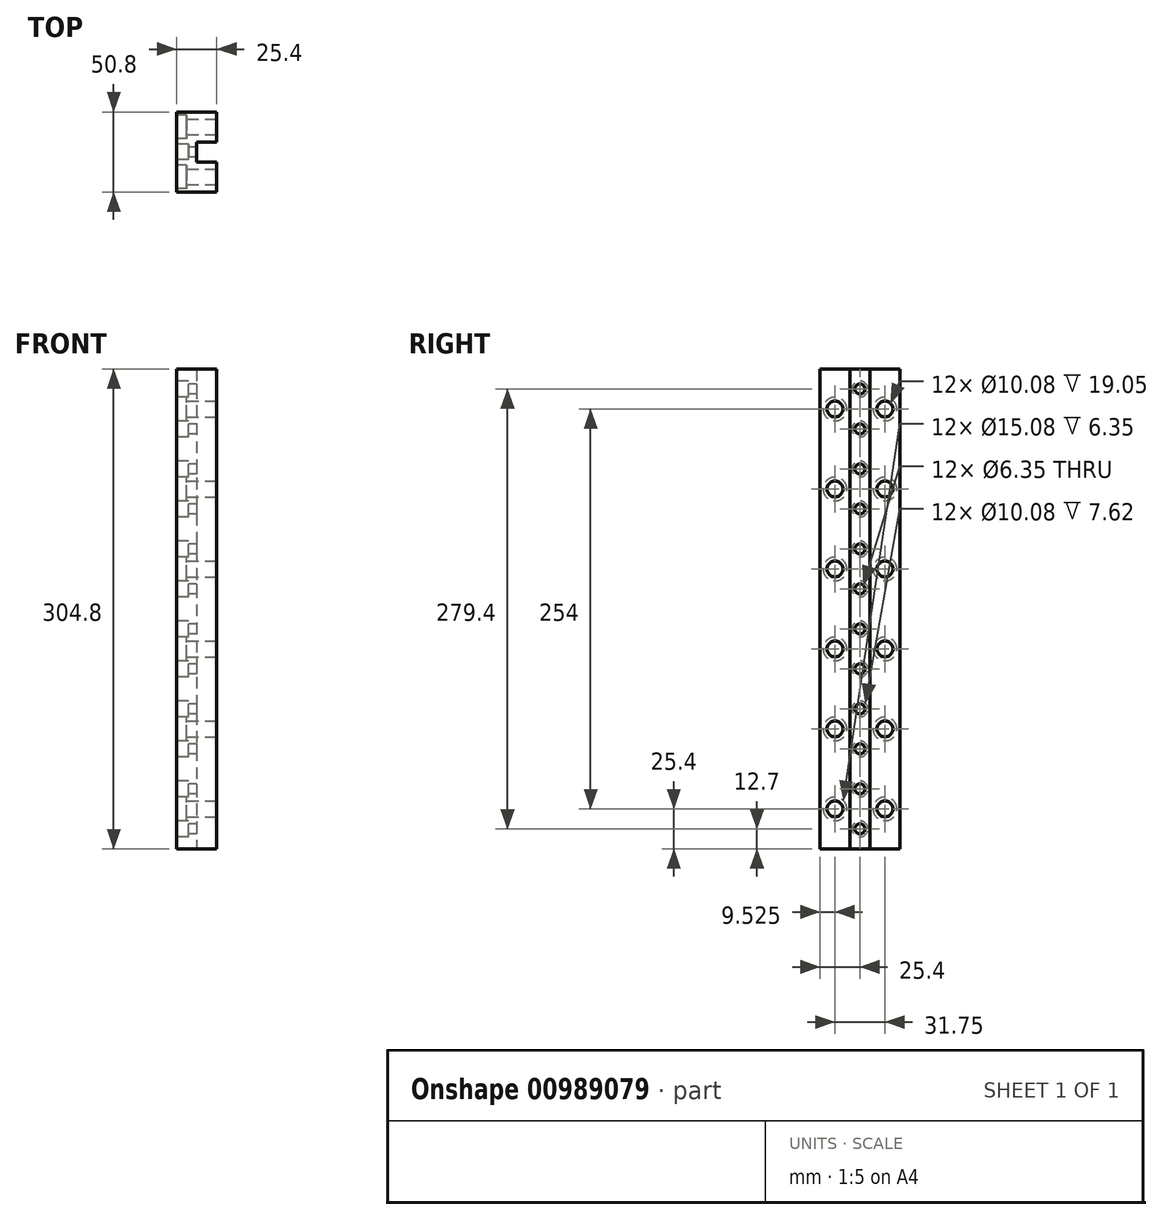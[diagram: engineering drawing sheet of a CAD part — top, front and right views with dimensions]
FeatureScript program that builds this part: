
annotation { "Feature Type Name" : "Feature", "Feature Type Description" : "" }
export const myFeature = defineFeature(function(context is Context, id is Id, definition is map)
    precondition{}
    {
        {
            var Q0;
            Q0=qCreatedBy(makeId("Right.planeOp"),FACE);
            var sketch = newSketch(context, id + "F0", { "sketchPlane" : qUnion([Q0])});
            skLineSegment(sketch, "E0.bottom", {"start": v(-25.4, 152.4) * mm, "end": v(25.4, 152.4) * mm});
            skLineSegment(sketch, "E0.top", {"start": v(-25.4, -152.4) * mm, "end": v(25.4, -152.4) * mm});
            skLineSegment(sketch, "E0.left", {"start": v(-25.4, 152.4) * mm, "end": v(-25.4, -152.4) * mm});
            skLineSegment(sketch, "E0.right", {"start": v(25.4, 152.4) * mm, "end": v(25.4, -152.4) * mm});
            skPoint(sketch, "E0.middle", {"position": v(0, 0) * mm});
            skSolve(sketch);
        }
        {
            var Q0;
            Q0 = qSketchRegion(id + "F0", true);
            extrude(context, id + "F1", {"entities" : qUnion([Q0]), "endBound" : BoundingType.SYMMETRIC, "depth" : 25.4 * mm, "offsetDistance" : 25.4 * mm});
        }
        {
            var Q0;
            Q0=qCreatedBy(makeId("Top.planeOp"),FACE);
            cPlane(context, id + "F2", {"entities" : qUnion([Q0]), "cplaneType" : CPlaneType.OFFSET, "offset" : 152.4 * mm, "oppositeDirection" : true, "width" : 152.4 * mm, "height" : 152.4 * mm});
        }
        {
            var Q0;
            Q0=qCreatedBy(id+"F2.planeOp",FACE);
            var sketch = newSketch(context, id + "F3", { "sketchPlane" : qUnion([Q0])});
            skLineSegment(sketch, "E1.bottom", {"start": v(12.7, -6.35) * mm, "end": v(0, -6.35) * mm});
            skLineSegment(sketch, "E1.top", {"start": v(12.7, 6.35) * mm, "end": v(0, 6.35) * mm});
            skLineSegment(sketch, "E1.left", {"start": v(12.7, -6.35) * mm, "end": v(12.7, 6.35) * mm});
            skLineSegment(sketch, "E1.right", {"start": v(0, -6.35) * mm, "end": v(0, 6.35) * mm});
            skPoint(sketch, "E2", {"position": v(0, -25.4) * mm});
            skPoint(sketch, "E3", {"position": v(0, 25.4) * mm});
            skSolve(sketch);
        }
        {
            var Q0;
            Q0 = qSketchRegion(id + "F3", true);
            extrude(context, id + "F4", {"entities" : qUnion([Q0]), "operationType" : NewBodyOperationType.REMOVE, "depth" : 304.8 * mm, "offsetDistance" : 25.4 * mm});
        }
        {
            var Q0;
            Q0=qCreatedBy(makeId("Right.planeOp"),FACE);
            cPlane(context, id + "F5", {"entities" : qUnion([Q0]), "cplaneType" : CPlaneType.OFFSET, "offset" : 12.7 * mm, "width" : 152.4 * mm, "height" : 152.4 * mm});
        }
        {
            var Q0;
            Q0=qCreatedBy(id+"F5.planeOp",FACE);
            var sketch = newSketch(context, id + "F6", { "sketchPlane" : qUnion([Q0])});
            skPoint(sketch, "E4", {"position": v(-25.4, -152.4) * mm});
            skPoint(sketch, "E5", {"position": v(-6.35, -152.4) * mm});
            skPoint(sketch, "E6", {"position": v(6.35, -152.4) * mm});
            skPoint(sketch, "E7", {"position": v(25.4, -152.4) * mm});
            skPoint(sketch, "E8", {"position": v(-25.4, -101.6) * mm});
            skPoint(sketch, "E9", {"position": v(-6.35, -101.6) * mm});
            skPoint(sketch, "E10", {"position": v(6.35, -101.6) * mm});
            skPoint(sketch, "E11", {"position": v(25.4, -101.6) * mm});
            skPoint(sketch, "E12", {"position": v(-25.4, -50.8) * mm});
            skPoint(sketch, "E13", {"position": v(-6.35, -50.8) * mm});
            skPoint(sketch, "E14", {"position": v(6.35, -50.8) * mm});
            skPoint(sketch, "E15", {"position": v(25.4, -50.8) * mm});
            skPoint(sketch, "E16", {"position": v(-25.4, 0) * mm});
            skPoint(sketch, "E17", {"position": v(-6.35, 0) * mm});
            skPoint(sketch, "E18", {"position": v(6.35, 0) * mm});
            skPoint(sketch, "E19", {"position": v(25.4, 0) * mm});
            skPoint(sketch, "E20", {"position": v(-25.4, 50.8) * mm});
            skPoint(sketch, "E21", {"position": v(-6.35, 50.8) * mm});
            skPoint(sketch, "E22", {"position": v(6.35, 50.8) * mm});
            skPoint(sketch, "E23", {"position": v(25.4, 50.8) * mm});
            skPoint(sketch, "E24", {"position": v(-25.4, 101.6) * mm});
            skPoint(sketch, "E25", {"position": v(-6.35, 101.6) * mm});
            skPoint(sketch, "E26", {"position": v(6.35, 101.6) * mm});
            skPoint(sketch, "E27", {"position": v(25.4, 101.6) * mm});
            skPoint(sketch, "E28", {"position": v(-15.88, -76.2) * mm});
            skPoint(sketch, "E29", {"position": v(-15.88, -25.4) * mm});
            skPoint(sketch, "E30", {"position": v(-15.88, 25.4) * mm});
            skPoint(sketch, "E31", {"position": v(-15.88, 76.2) * mm});
            skPoint(sketch, "E32", {"position": v(15.87, 76.2) * mm});
            skPoint(sketch, "E33", {"position": v(15.87, 25.4) * mm});
            skPoint(sketch, "E34", {"position": v(15.87, -25.4) * mm});
            skPoint(sketch, "E35", {"position": v(15.87, -76.2) * mm});
            skPoint(sketch, "E36", {"position": v(-15.88, -127) * mm});
            skPoint(sketch, "E37", {"position": v(-15.88, -152.4) * mm});
            skPoint(sketch, "E38", {"position": v(15.87, -127) * mm});
            skPoint(sketch, "E39", {"position": v(15.87, -152.4) * mm});
            skPoint(sketch, "E40", {"position": v(-15.88, 127) * mm});
            skPoint(sketch, "E41", {"position": v(15.87, 127) * mm});
            skSolve(sketch);
        }
        {
            var Q0;
            Q0=sQuery(id+"F6.wireOp",VERTEX,"d55c85b4-804a-40fe-89ae-485f87a3ce57");
            var Q1;
            Q1=sQuery(id+"F6.wireOp",VERTEX,"4aae8de5-d04d-4cfe-9f82-e7af8451480e");
            var Q2;
            Q2=sQuery(id+"F6.wireOp",VERTEX,"14c4b5a4-c554-4fe2-9cf0-08c26e14d046");
            var Q3;
            Q3=sQuery(id+"F6.wireOp",VERTEX,"b5e11202-0810-44d7-ac35-54ce5016bb80");
            var Q4;
            Q4=sQuery(id+"F6.wireOp",VERTEX,"21e4fa36-830b-4be3-85d7-d00b1b71e43a");
            var Q5;
            Q5=sQuery(id+"F6.wireOp",VERTEX,"086ac343-482b-45e4-8ac3-c1544311829b");
            var Q6;
            Q6=sQuery(id+"F6.wireOp",VERTEX,"6163d127-73d7-440f-8c50-218c48537137");
            var Q7;
            Q7=sQuery(id+"F6.wireOp",VERTEX,"6c5e894b-45dd-4a6c-a4cd-9d038fab3ba1");
            var Q8;
            Q8=sQuery(id+"F6.wireOp",VERTEX,"e5a3135e-7f6b-4397-8038-c7202fe8f8f5");
            var Q9;
            Q9=sQuery(id+"F6.wireOp",VERTEX,"4baa1079-f2f2-408e-9dee-b537d3760503");
            var Q10;
            Q10=sQuery(id+"F6.wireOp",VERTEX,"E31");
            var Q11;
            Q11=sQuery(id+"F6.wireOp",VERTEX,"E32");
            var Q12;
            Q12=sQuery(id+"F6.wireOp",VERTEX,"E33");
            var Q13;
            Q13=sQuery(id+"F6.wireOp",VERTEX,"E30");
            var Q14;
            Q14=sQuery(id+"F6.wireOp",VERTEX,"E29");
            var Q15;
            Q15=sQuery(id+"F6.wireOp",VERTEX,"E34");
            var Q16;
            Q16=sQuery(id+"F6.wireOp",VERTEX,"E38");
            var Q17;
            Q17=sQuery(id+"F6.wireOp",VERTEX,"E36");
            var Q18;
            Q18=sQuery(id+"F6.wireOp",VERTEX,"E28");
            var Q19;
            Q19=sQuery(id+"F6.wireOp",VERTEX,"E35");
            var Q20;
            Q20=sQuery(id+"F6.wireOp",VERTEX,"E40");
            var Q21;
            Q21=sQuery(id+"F6.wireOp",VERTEX,"E41");
            var Q22;
            Q22=makeQuery(id+"F1.opExtrude","SWEPT_BODY",BODY,{"disambiguationData":[OSD([sQuery(id+"F0.wireOp",EDGE,"E0.bottom"),sQuery(id+"F0.wireOp",EDGE,"E0.top"),sQuery(id+"F0.wireOp",EDGE,"E0.left"),sQuery(id+"F0.wireOp",EDGE,"E0.right")])]});
            hole(context, id + "F7", {"style" : HoleStyle.SIMPLE, "endStyle" : HoleEndStyle.BLIND, "holeDiameter" : 10.08 * mm, "majorDiameter" : 6.35 * mm, "holeDepth" : 30.48 * mm, "isTappedThrough" : true, "tappedDepth" : 12.7 * mm, "tapClearance" : 3, "locations" : qUnion([Q0, Q1, Q2, Q3, Q4, Q5, Q6, Q7, Q8, Q9, Q10, Q11, Q12, Q13, Q14, Q15, Q16, Q17, Q18, Q19, Q20, Q21]), "scope" : qUnion([Q22])});
        }
        {
            var Q0;
            Q0=qCreatedBy(id+"F5.planeOp",FACE);
            cPlane(context, id + "F8", {"entities" : qUnion([Q0]), "cplaneType" : CPlaneType.OFFSET, "offset" : 25.4 * mm, "oppositeDirection" : true, "width" : 152.4 * mm, "height" : 152.4 * mm});
        }
        {
            var Q0;
            Q0=qCreatedBy(id+"F8.planeOp",FACE);
            var sketch = newSketch(context, id + "F9", { "sketchPlane" : qUnion([Q0])});
            skPoint(sketch, "E42", {"position": v(15.87, 127) * mm});
            skPoint(sketch, "E43", {"position": v(-15.88, 127) * mm});
            skPoint(sketch, "E44", {"position": v(-15.88, 76.2) * mm});
            skPoint(sketch, "E45", {"position": v(15.87, 76.2) * mm});
            skPoint(sketch, "E46", {"position": v(15.87, 25.4) * mm});
            skPoint(sketch, "E47", {"position": v(-15.88, 25.4) * mm});
            skPoint(sketch, "E48", {"position": v(-15.88, -25.4) * mm});
            skPoint(sketch, "E49", {"position": v(15.87, -25.4) * mm});
            skPoint(sketch, "E50", {"position": v(15.87, -76.2) * mm});
            skPoint(sketch, "E51", {"position": v(-15.88, -76.2) * mm});
            skPoint(sketch, "E52", {"position": v(-15.88, -127) * mm});
            skPoint(sketch, "E53", {"position": v(15.87, -127) * mm});
            skCircle(sketch, "E54", {"center": v(15.87, 127) * mm, "radius": 7.54 * mm});
            skCircle(sketch, "E55", {"center": v(-15.88, 127) * mm, "radius": 7.54 * mm});
            skCircle(sketch, "E56", {"center": v(-15.88, 76.2) * mm, "radius": 7.54 * mm});
            skCircle(sketch, "E57", {"center": v(15.87, 76.2) * mm, "radius": 7.54 * mm});
            skCircle(sketch, "E58", {"center": v(15.87, 25.4) * mm, "radius": 7.54 * mm});
            skCircle(sketch, "E59", {"center": v(-15.88, 25.4) * mm, "radius": 7.54 * mm});
            skCircle(sketch, "E60", {"center": v(15.87, -25.4) * mm, "radius": 7.54 * mm});
            skCircle(sketch, "E61", {"center": v(-15.88, -25.4) * mm, "radius": 7.54 * mm});
            skCircle(sketch, "E62", {"center": v(-15.88, -76.2) * mm, "radius": 7.54 * mm});
            skCircle(sketch, "E63", {"center": v(15.87, -76.2) * mm, "radius": 7.54 * mm});
            skCircle(sketch, "E64", {"center": v(15.87, -127) * mm, "radius": 7.54 * mm});
            skCircle(sketch, "E65", {"center": v(-15.88, -127) * mm, "radius": 7.54 * mm});
            skCircle(sketch, "E66", {"center": v(15.87, 127) * mm, "radius": 3.3 * mm});
            skCircle(sketch, "E67", {"center": v(-15.88, 127) * mm, "radius": 3.3 * mm});
            skCircle(sketch, "E68", {"center": v(-15.88, 76.2) * mm, "radius": 3.3 * mm});
            skCircle(sketch, "E69", {"center": v(15.87, 76.2) * mm, "radius": 3.3 * mm});
            skCircle(sketch, "E70", {"center": v(15.87, 25.4) * mm, "radius": 3.3 * mm});
            skCircle(sketch, "E71", {"center": v(-15.88, 25.4) * mm, "radius": 3.3 * mm});
            skCircle(sketch, "E72", {"center": v(-15.88, -25.4) * mm, "radius": 3.3 * mm});
            skCircle(sketch, "E73", {"center": v(15.87, -25.4) * mm, "radius": 3.3 * mm});
            skCircle(sketch, "E74", {"center": v(15.87, -76.2) * mm, "radius": 3.3 * mm});
            skCircle(sketch, "E75", {"center": v(-15.88, -76.2) * mm, "radius": 3.3 * mm});
            skCircle(sketch, "E76", {"center": v(-15.88, -127) * mm, "radius": 3.3 * mm});
            skCircle(sketch, "E77", {"center": v(15.87, -127) * mm, "radius": 3.3 * mm});
            skSolve(sketch);
        }
        {
            var Q0;
            Q0 = qSketchRegion(id + "F9", true);
            extrude(context, id + "F10", {"entities" : qUnion([Q0]), "operationType" : NewBodyOperationType.REMOVE, "depth" : 6.35 * mm, "offsetDistance" : 25.4 * mm});
        }
        {
            var Q0;
            Q0=qCreatedBy(id+"F8.planeOp",FACE);
            var sketch = newSketch(context, id + "F11", { "sketchPlane" : qUnion([Q0])});
            skPoint(sketch, "E78", {"position": v(0, -152.4) * mm});
            skPoint(sketch, "E79", {"position": v(0, -139.7) * mm});
            skPoint(sketch, "E80", {"position": v(0, -114.3) * mm});
            skPoint(sketch, "E81", {"position": v(0, -88.9) * mm});
            skPoint(sketch, "E82", {"position": v(0, -63.5) * mm});
            skPoint(sketch, "E83", {"position": v(0, -38.1) * mm});
            skPoint(sketch, "E84", {"position": v(0, -12.7) * mm});
            skPoint(sketch, "E85", {"position": v(0, 12.7) * mm});
            skPoint(sketch, "E86", {"position": v(0, 38.1) * mm});
            skPoint(sketch, "E87", {"position": v(0, 63.5) * mm});
            skPoint(sketch, "E88", {"position": v(0, 88.9) * mm});
            skPoint(sketch, "E89", {"position": v(0, 114.3) * mm});
            skPoint(sketch, "E90", {"position": v(0, 139.7) * mm});
            skSolve(sketch);
        }
        {
            var Q0;
            Q0=sQuery(id+"F11.wireOp",VERTEX,"E90");
            var Q1;
            Q1=sQuery(id+"F11.wireOp",VERTEX,"E89");
            var Q2;
            Q2=sQuery(id+"F11.wireOp",VERTEX,"E88");
            var Q3;
            Q3=sQuery(id+"F11.wireOp",VERTEX,"E87");
            var Q4;
            Q4=sQuery(id+"F11.wireOp",VERTEX,"E86");
            var Q5;
            Q5=sQuery(id+"F11.wireOp",VERTEX,"E84");
            var Q6;
            Q6=sQuery(id+"F11.wireOp",VERTEX,"E85");
            var Q7;
            Q7=sQuery(id+"F11.wireOp",VERTEX,"E83");
            var Q8;
            Q8=sQuery(id+"F11.wireOp",VERTEX,"E82");
            var Q9;
            Q9=sQuery(id+"F11.wireOp",VERTEX,"E80");
            var Q10;
            Q10=sQuery(id+"F11.wireOp",VERTEX,"E79");
            var Q11;
            Q11=sQuery(id+"F11.wireOp",VERTEX,"E81");
            var Q12;
            Q12=makeQuery(id+"F1.opExtrude","SWEPT_BODY",BODY,{"disambiguationData":[OSD([sQuery(id+"F0.wireOp",EDGE,"E0.bottom"),sQuery(id+"F0.wireOp",EDGE,"E0.top"),sQuery(id+"F0.wireOp",EDGE,"E0.left"),sQuery(id+"F0.wireOp",EDGE,"E0.right")])]});
            hole(context, id + "F12", {"style" : HoleStyle.SIMPLE, "endStyle" : HoleEndStyle.BLIND, "oppositeDirection" : true, "holeDiameter" : 6.35 * mm, "majorDiameter" : 6.35 * mm, "holeDepth" : 30.48 * mm, "isTappedThrough" : true, "tappedDepth" : 12.7 * mm, "tapClearance" : 3, "locations" : qUnion([Q0, Q1, Q2, Q3, Q4, Q5, Q6, Q7, Q8, Q9, Q10, Q11]), "scope" : qUnion([Q12])});
        }
        {
            var Q0;
            Q0=qCreatedBy(id+"F8.planeOp",FACE);
            var sketch = newSketch(context, id + "F13", { "sketchPlane" : qUnion([Q0])});
            skPoint(sketch, "E91", {"position": v(0, -139.7) * mm});
            skPoint(sketch, "E92", {"position": v(0, -114.3) * mm});
            skPoint(sketch, "E93", {"position": v(0, -88.9) * mm});
            skPoint(sketch, "E94", {"position": v(0, -63.5) * mm});
            skPoint(sketch, "E95", {"position": v(0, -38.1) * mm});
            skPoint(sketch, "E96", {"position": v(0, -12.7) * mm});
            skPoint(sketch, "E97", {"position": v(0, 12.7) * mm});
            skPoint(sketch, "E98", {"position": v(0, 38.1) * mm});
            skPoint(sketch, "E99", {"position": v(0, 63.5) * mm});
            skPoint(sketch, "E100", {"position": v(0, 88.9) * mm});
            skPoint(sketch, "E101", {"position": v(0, 114.3) * mm});
            skPoint(sketch, "E102", {"position": v(0, 139.7) * mm});
            skCircle(sketch, "E103", {"center": v(0, 139.7) * mm, "radius": 5.04 * mm});
            skCircle(sketch, "E104", {"center": v(0, 114.3) * mm, "radius": 5.04 * mm});
            skCircle(sketch, "E105", {"center": v(0, 88.9) * mm, "radius": 5.04 * mm});
            skCircle(sketch, "E106", {"center": v(0, 63.5) * mm, "radius": 5.04 * mm});
            skCircle(sketch, "E107", {"center": v(0, 38.1) * mm, "radius": 5.04 * mm});
            skCircle(sketch, "E108", {"center": v(0, 12.7) * mm, "radius": 5.04 * mm});
            skCircle(sketch, "E109", {"center": v(0, -12.7) * mm, "radius": 5.04 * mm});
            skCircle(sketch, "E110", {"center": v(0, -38.1) * mm, "radius": 5.04 * mm});
            skCircle(sketch, "E111", {"center": v(0, -63.5) * mm, "radius": 5.04 * mm});
            skCircle(sketch, "E112", {"center": v(0, -88.9) * mm, "radius": 5.04 * mm});
            skCircle(sketch, "E113", {"center": v(0, -114.3) * mm, "radius": 5.04 * mm});
            skCircle(sketch, "E114", {"center": v(0, -139.7) * mm, "radius": 5.04 * mm});
            skCircle(sketch, "E115", {"center": v(0, -139.7) * mm, "radius": 2.54 * mm});
            skCircle(sketch, "E116", {"center": v(0, -114.3) * mm, "radius": 2.54 * mm});
            skCircle(sketch, "E117", {"center": v(0, -88.9) * mm, "radius": 2.54 * mm});
            skCircle(sketch, "E118", {"center": v(0, -63.5) * mm, "radius": 2.54 * mm});
            skCircle(sketch, "E119", {"center": v(0, -38.1) * mm, "radius": 2.54 * mm});
            skCircle(sketch, "E120", {"center": v(0, -12.7) * mm, "radius": 2.54 * mm});
            skCircle(sketch, "E121", {"center": v(0, 12.7) * mm, "radius": 2.54 * mm});
            skCircle(sketch, "E122", {"center": v(0, 38.1) * mm, "radius": 2.54 * mm});
            skCircle(sketch, "E123", {"center": v(0, 63.5) * mm, "radius": 2.54 * mm});
            skCircle(sketch, "E124", {"center": v(0, 88.9) * mm, "radius": 2.54 * mm});
            skCircle(sketch, "E125", {"center": v(0, 114.3) * mm, "radius": 2.54 * mm});
            skCircle(sketch, "E126", {"center": v(0, 139.7) * mm, "radius": 2.54 * mm});
            skSolve(sketch);
        }
        {
            var Q0;
            Q0 = qSketchRegion(id + "F13", true);
            extrude(context, id + "F14", {"entities" : qUnion([Q0]), "operationType" : NewBodyOperationType.REMOVE, "depth" : 7.62 * mm, "offsetDistance" : 25.4 * mm});
        }
    });
